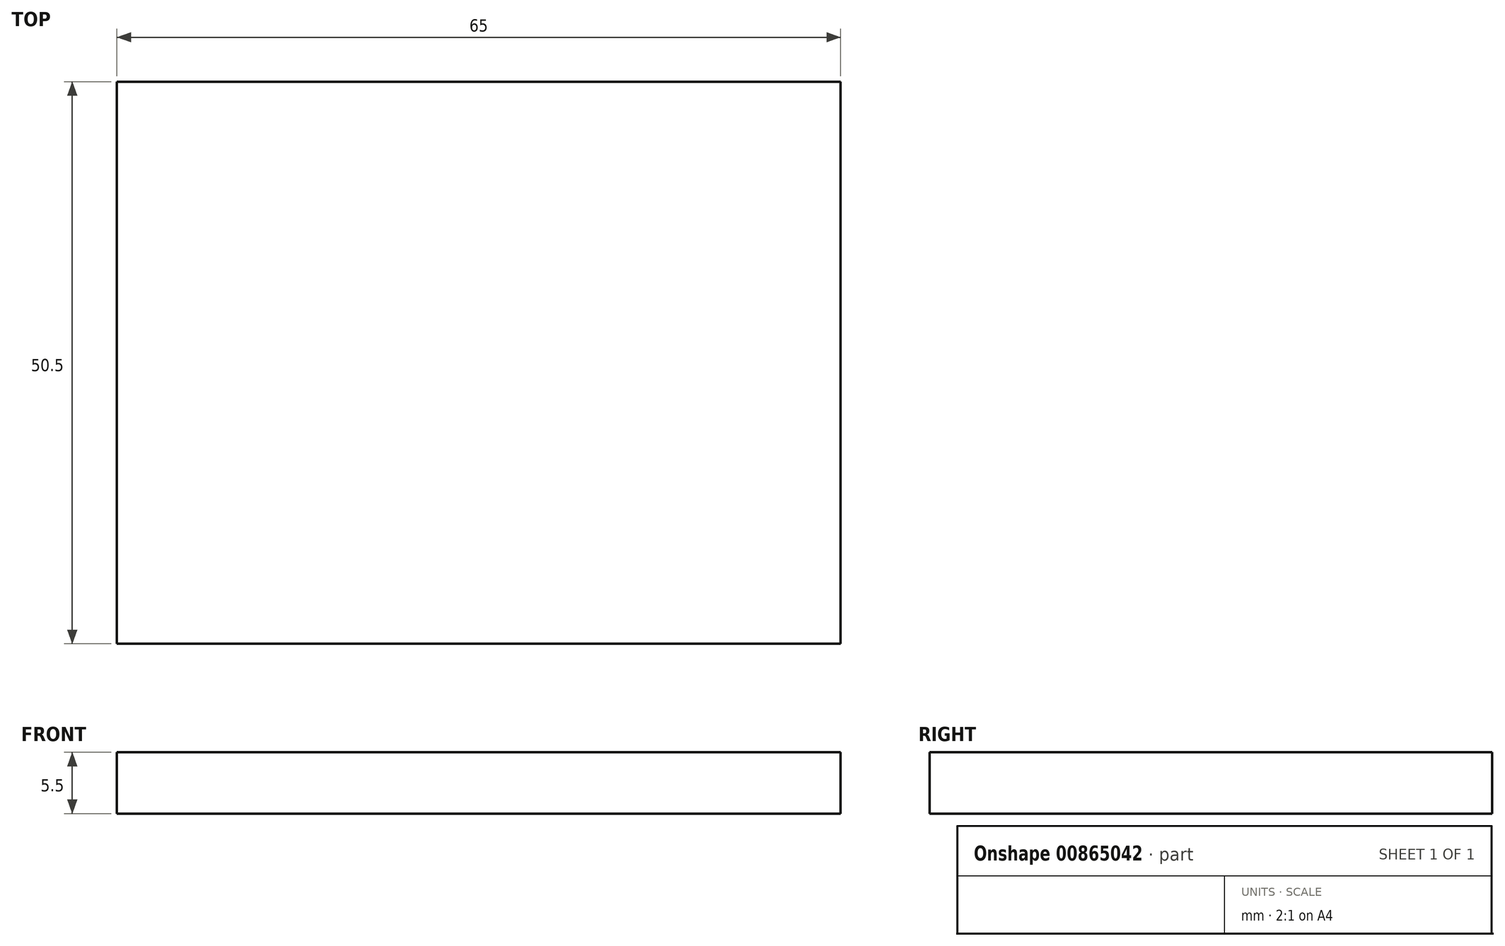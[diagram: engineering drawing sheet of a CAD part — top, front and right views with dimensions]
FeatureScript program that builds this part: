
annotation { "Feature Type Name" : "Feature", "Feature Type Description" : "" }
export const myFeature = defineFeature(function(context is Context, id is Id, definition is map)
    precondition{}
    {
        {
            var Q0;
            Q0=qCreatedBy(makeId("Top.planeOp"),FACE);
            var sketch = newSketch(context, id + "F0", { "sketchPlane" : qUnion([Q0])});
            skLineSegment(sketch, "E0.bottom", {"start": v(32.5, -25.25) * mm, "end": v(-32.5, -25.25) * mm});
            skLineSegment(sketch, "E0.top", {"start": v(32.5, 25.25) * mm, "end": v(-32.5, 25.25) * mm});
            skLineSegment(sketch, "E0.left", {"start": v(32.5, -25.25) * mm, "end": v(32.5, 25.25) * mm});
            skLineSegment(sketch, "E0.right", {"start": v(-32.5, -25.25) * mm, "end": v(-32.5, 25.25) * mm});
            skPoint(sketch, "E0.middle", {"position": v(0, 0) * mm});
            skSolve(sketch);
        }
        {
            var Q0;
            Q0=makeQuery(id+"F0.imprint","IMPRINT",FACE,{"disambiguationData":[TD([[makeQuery(id+"F0.imprint","IMPRINT",EDGE,{"derivedFrom":sQuery(id+"F0.wireOp",EDGE,"E0.bottom")}),-1.0]])]});
            extrude(context, id + "F1", {"entities" : qUnion([Q0]), "depth" : 5.5 * mm, "offsetDistance" : 25 * mm});
        }
    });
